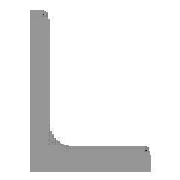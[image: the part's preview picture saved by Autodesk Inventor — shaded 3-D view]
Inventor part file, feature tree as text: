
AUTODESK INVENTOR PART (.ipt)
format: ipt  version: 2024.1 (Build 281209000, 209)  size: 120,320 bytes
history: native  units: mm (DEFAULTED — no unit token found)
features: other x4, sketch x1, plane x1
ambient origin geometry x8: Origin, YZ Plane, XZ Plane, XY Plane, X Axis, Y Axis, Z Axis, Center Point
bodies: Solid1 (feature_tree), Body (feature_tree)
feature tree (6):
  parser-record x1  (decoder bookkeeping rows leaked as tree rows — omitted from the tree; the rows remain in map.json)
  other  "Driven Length"
  other  "Start Plane"
  other  "End Plane"
  sketch  "Sketch3"  dims[d0=25.4mm d1=25.4mm d2=3.175mm d3=3.175mm d4=1200.0mm d5=0.0mm d10=0.0mm d11=0.0mm d12=-0.0mm d13=1200.0mm d14=3.302mm d15=1.524mm d16=90.0deg d17=1200.0mm]
  plane  "Work Plane3"
